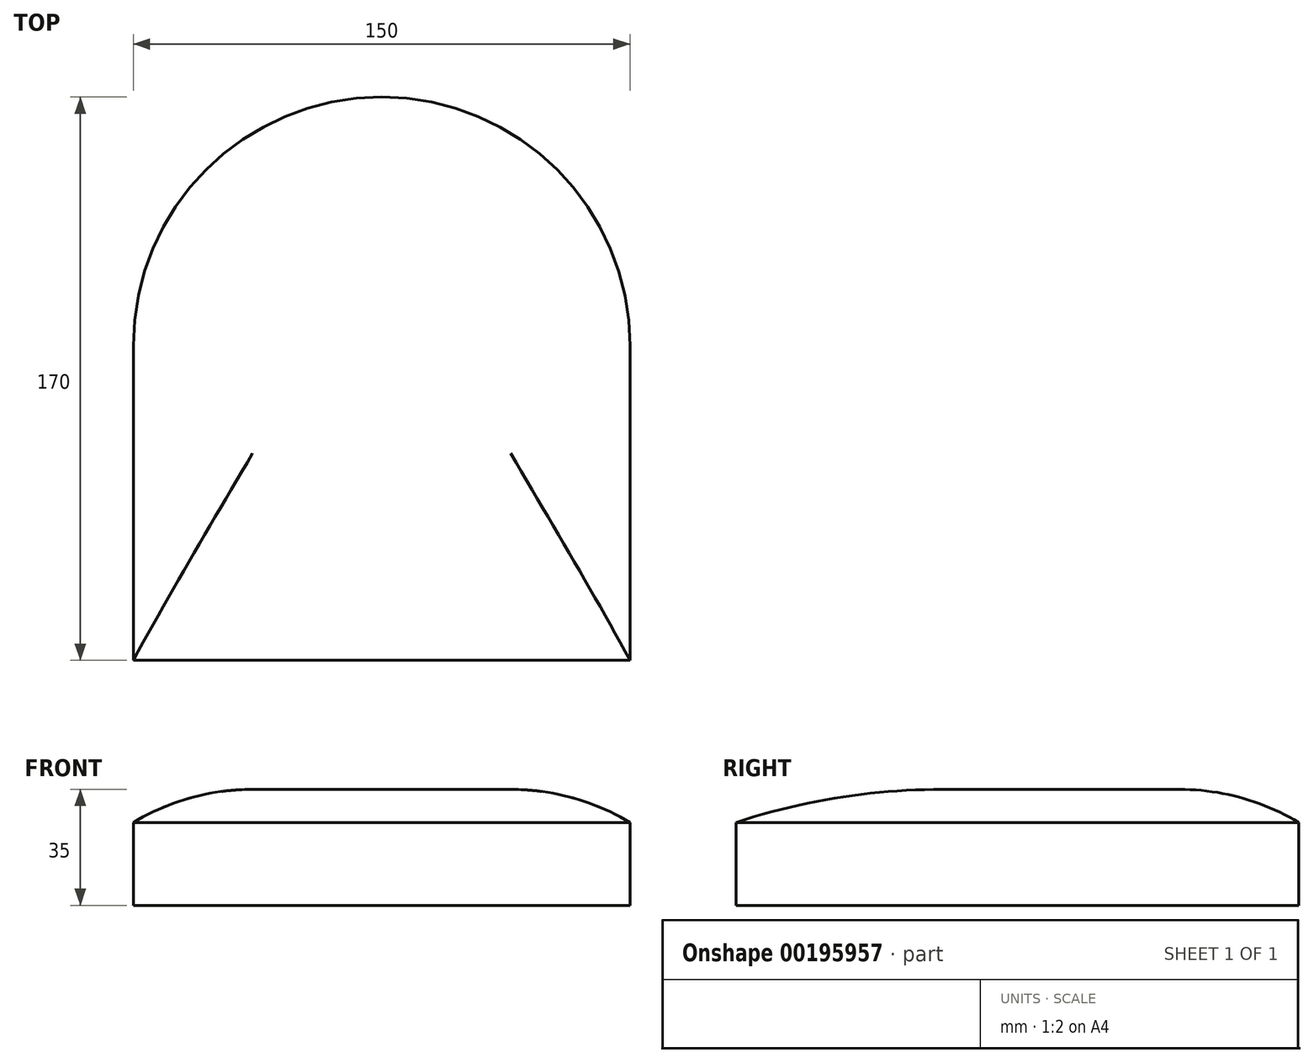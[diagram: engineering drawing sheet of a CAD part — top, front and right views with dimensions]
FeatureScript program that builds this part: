
annotation { "Feature Type Name" : "Feature", "Feature Type Description" : "" }
export const myFeature = defineFeature(function(context is Context, id is Id, definition is map)
    precondition{}
    {
        {
            var Q0;
            Q0=qCreatedBy(makeId("Top.planeOp"),FACE);
            var sketch = newSketch(context, id + "F0", { "sketchPlane" : qUnion([Q0])});
            skCircle(sketch, "E0", {"center": v(0, 0) * mm, "radius": 75 * mm});
            skLineSegment(sketch, "E1.bottom", {"start": v(-75, 0) * mm, "end": v(75, 0) * mm});
            skLineSegment(sketch, "E1.top", {"start": v(-75, -95) * mm, "end": v(75, -95) * mm});
            skLineSegment(sketch, "E1.left", {"start": v(-75, 0) * mm, "end": v(-75, -95) * mm});
            skLineSegment(sketch, "E1.right", {"start": v(75, 0) * mm, "end": v(75, -95) * mm});
            skSolve(sketch);
        }
        {
            var Q0;
            Q0 = qSketchRegion(id + "F0", true);
            extrude(context, id + "F1", {"entities" : qUnion([Q0]), "depth" : 10 * mm});
        }
        {
            var Q0;
            Q0=makeQuery(id+"F1.opExtrude","CAP_EDGE",EDGE,{"disambiguationData":[OSD([sQuery(id+"F0.wireOp",EDGE,"E1.top")])],"isStart":false});
            fillet(context, id + "F2", {"entities" : qUnion([Q0]), "radius" : 200 * mm, "tangentPropagation" : true, "allowEdgeOverflow" : false});
        }
        {
            var Q0;
            Q0=makeQuery(id+"F1.opExtrude","CAP_EDGE",EDGE,{"disambiguationData":[OSD([sQuery(id+"F0.wireOp",EDGE,"E0")])],"isStart":false});
            fillet(context, id + "F3", {"entities" : qUnion([Q0]), "radius" : 70 * mm, "tangentPropagation" : true, "allowEdgeOverflow" : false});
        }
        {
            var Q0;
            Q0=makeQuery(id+"F1.opExtrude","CAP_FACE",FACE,{"disambiguationData":[OSD([sQuery(id+"F0.wireOp",EDGE,"E0"),sQuery(id+"F0.wireOp",EDGE,"E1.top"),sQuery(id+"F0.wireOp",EDGE,"E1.left"),sQuery(id+"F0.wireOp",EDGE,"E1.right")])],"isStart":true});
            extrude(context, id + "F4", {"entities" : qUnion([Q0]), "operationType" : NewBodyOperationType.ADD, "depth" : 25 * mm});
        }
    });
